# Revit family: LC Mini 120 Sans hôte
name_source: partatom
category: Dispositifs d'éclairage
units: mm (PartAtom-declared; Revit-internal decimal feet)

## family parameters
Basée sur le plan de construction = Non
Conserver l'orientation des annotations = Non
Cote de connecteur circulaire = Utiliser le diamètre
Couper avec des vides une fois chargée = Non
Partagée = Non
Point de calcul de pièce = Non
Toujours verticalement = Oui
Type d'élément = Normal

## types (5) — shared parameters
Classe = II
Code d'assemblage = D5010200
Elévation par défaut = 250 cm
Fabricant = B.E.G.
Hauteur de montage max = 400 cm
IP = 44
Image du type = MURAL.JPG
Marque = LUXOMAT
Mode de pose = Mural
Position en hauteur = 250 cm
Température ambiante = -25°C à + 50°C
URL = http://www.luxomat.com

## per-type parameters (varying)
| type | Alimentation | Charge Cos ɸ =0.5 | Charge Cos ɸ =1 | Charge LED | Commentaires du type | Consommation | Modèle | Relais | Référence | Type de Sortie |
| 01- LC Mini 120 Générique | 110-240 V AC |  |  |  | MINI.DET.MOUV.120°/10M MURAL |  | LC Mini 120 |  |  |  |
| 02- LC Mini 120 réf 91051 | 110-240 V AC | 500 VA | 1000 W | 200 W | MINI.DET.MOUV.1 CONTACT.120°/10M MURAL | 0.4 W | LC Mini 120 | 4.3 A | 91051 | TOR |
| 03- LC Mini 120 DALILINK réf 93849 | 16 V DC par Bus DALI | 0 | 0 | 0 | MINI.MULTI.CAPTEUR.MOUV.DALILINK.120°/10M MURAL | 3 mA | LC Mini 120 DALILINK | 0 | 93849 | DALILINK |
| 04- LC Mini 120 DALISYS réf 93305 | 10-22 V DC par Bus DALI | 0 | 0 | 0 | MINI.MULTI.CAPTEUR.MOUV.DALISYS.120°/10M MURAL | 3 mA | LC Mini 120 DALISYS | 0 | 93305 | DALI Adressable |
| 05- LC Mini 120 BMS DALI 2 réf 93541 | 10-22 V DC par Bus DALI | 0 | 0 | 0 | MINI.MULTI.CAPTEUR.MOUV.BMS.DALI.2.120°/10M MURAL | 3 mA | LC Mini 120 BMS DALI 2 | 0 | 93541 | DALI 2 Adressable - BMS |
